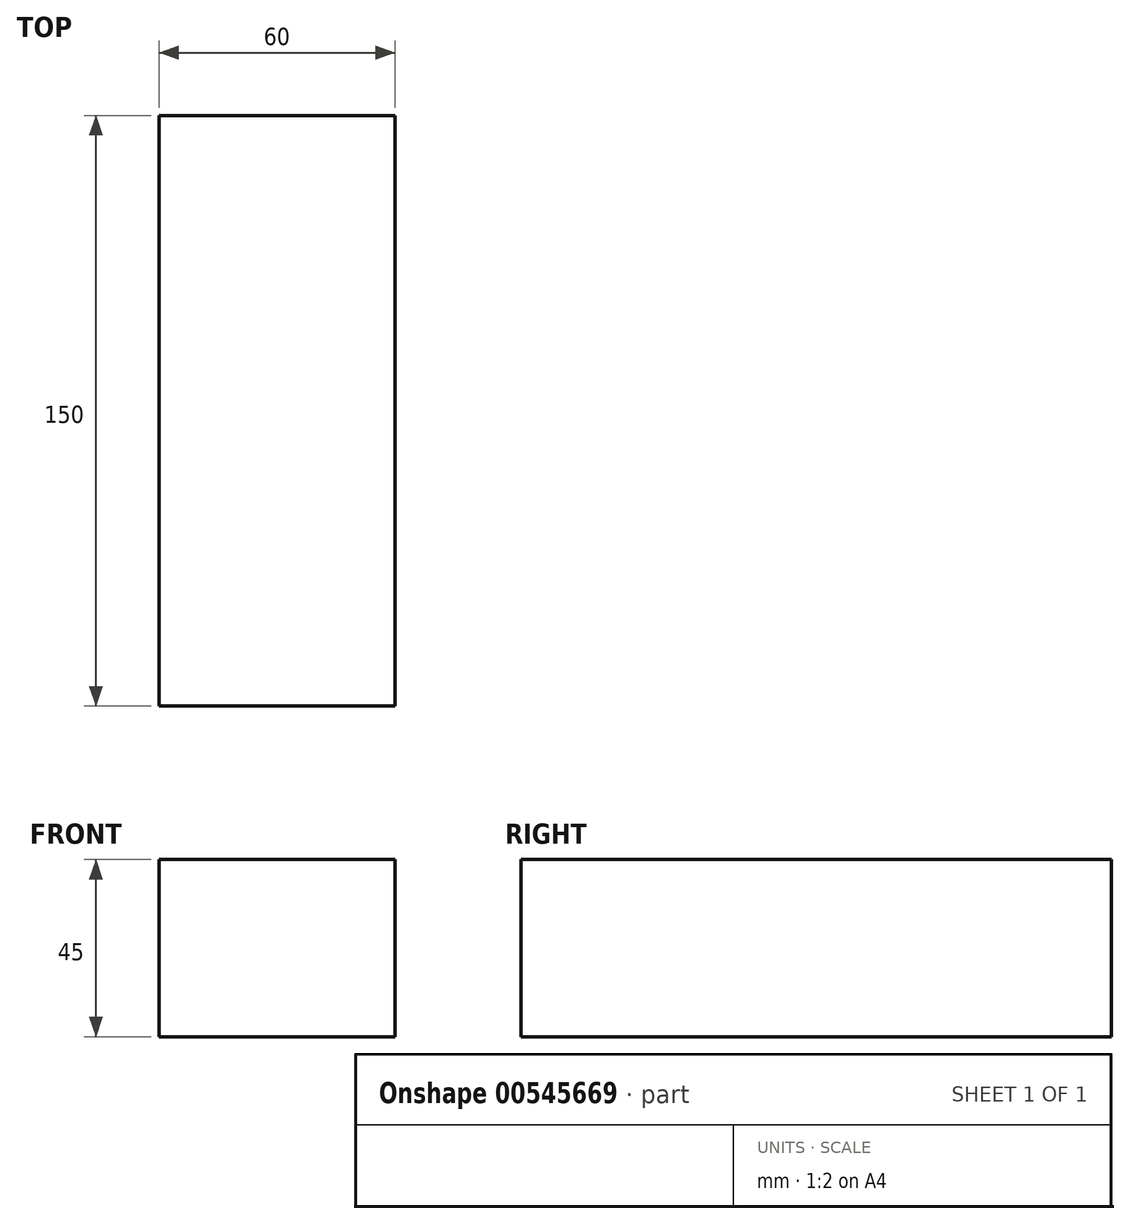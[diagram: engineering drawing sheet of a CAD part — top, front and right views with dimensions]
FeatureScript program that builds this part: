
annotation { "Feature Type Name" : "Feature", "Feature Type Description" : "" }
export const myFeature = defineFeature(function(context is Context, id is Id, definition is map)
    precondition{}
    {
        {
            var Q0;
            Q0=qCreatedBy(makeId("Top.planeOp"),FACE);
            var sketch = newSketch(context, id + "F0", { "sketchPlane" : qUnion([Q0])});
            skLineSegment(sketch, "E0.bottom", {"start": v(-42.48, 78.11) * mm, "end": v(17.52, 78.11) * mm});
            skLineSegment(sketch, "E0.top", {"start": v(-42.48, -71.89) * mm, "end": v(17.52, -71.89) * mm});
            skLineSegment(sketch, "E0.left", {"start": v(-42.48, 78.11) * mm, "end": v(-42.48, -71.89) * mm});
            skLineSegment(sketch, "E0.right", {"start": v(17.52, 78.11) * mm, "end": v(17.52, -71.89) * mm});
            skSolve(sketch);
        }
        {
            var Q0;
            Q0 = qSketchRegion(id + "F0", true);
            extrude(context, id + "F1", {"entities" : qUnion([Q0]), "oppositeDirection" : true, "depth" : 45 * mm, "offsetDistance" : 25 * mm});
        }
    });
